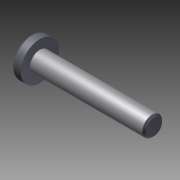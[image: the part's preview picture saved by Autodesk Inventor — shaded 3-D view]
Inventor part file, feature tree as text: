
AUTODESK INVENTOR PART (.ipt)
format: ipt  version: 2015 (Build 190159000, 159)  size: 124,928 bytes
history: native  units: in
note: dims shown in document units (in); Inventor stores cm internally (conversion verified against a paired STEP export)
features: chamfer x1, other x1, imported_body x1
ambient origin geometry x8: Origin, YZ Plane, XZ Plane, XY Plane, X Axis, Y Axis, Z Axis, Center Point
bodies: Body1 (feature_tree)
feature tree (3):
  chamfer  "Chamfer1"  [1 undecoded]
  other  "2-56 X 0.500 PHS (PHS-05)1"
  imported_body  "Base1"
note: 1 required parameter value undecoded (feature->parameter linkage not recoverable at this tier; creation-order binding heuristic only, values carry confidence <= 0.55)
